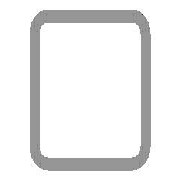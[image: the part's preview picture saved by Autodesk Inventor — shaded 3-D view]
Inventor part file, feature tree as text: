
AUTODESK INVENTOR PART (.ipt)
format: ipt  version: 2024.3 (Build 283343000, 343)  size: 159,232 bytes
history: native  units: mm (DEFAULTED — no unit token found)
features: other x4, plane x2, sketch x2, extrude x1, split x1
ambient origin geometry x8: Origin, YZ Plane, XZ Plane, XY Plane, X Axis, Y Axis, Z Axis, Center Point
bodies: Solid1 (feature_tree), Body (feature_tree)
feature tree (10):
  parser-record x1  (decoder bookkeeping rows leaked as tree rows — omitted from the tree; the rows remain in map.json)
  other  "Driven Length"
  other  "Start Plane"
  other  "End Plane"
  extrude  "Extrusion2"  TaperAngle=0.0deg  [1 undecoded]
  plane  "Work Plane5"
  split  "Split2"
  sketch  "Sketch3"  dims[d3=350.0mm d4=0.0mm]
  plane  "Work Plane3"
  sketch  "Sketch5"  dims[d7=6.0mm d9=100.0mm d11=100.0mm d12=3.0mm d13=-50.0mm d14=300.0mm d15=50.0mm d16=50.0mm d17=90.0deg d18=350.0mm d19=100.0mm d20=10.0mm d21=0.0mm]
note: 1 required parameter value undecoded (feature->parameter linkage not recoverable at this tier; creation-order binding heuristic only, values carry confidence <= 0.55)
